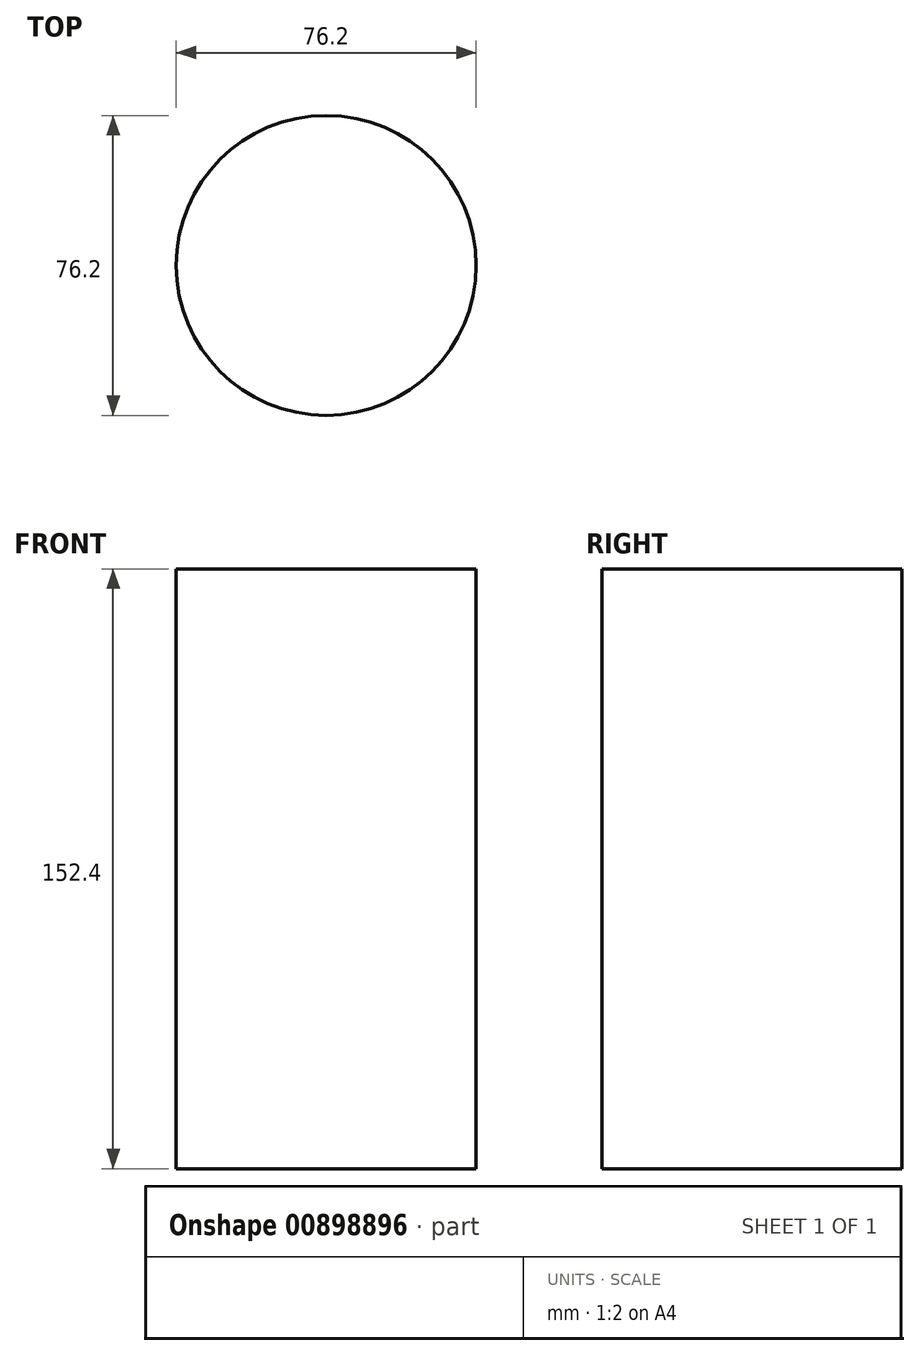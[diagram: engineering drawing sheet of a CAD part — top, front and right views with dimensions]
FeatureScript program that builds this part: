
annotation { "Feature Type Name" : "Feature", "Feature Type Description" : "" }
export const myFeature = defineFeature(function(context is Context, id is Id, definition is map)
    precondition{}
    {
        {
            var Q0;
            Q0=qCreatedBy(makeId("Top.planeOp"),FACE);
            var sketch = newSketch(context, id + "F0", { "sketchPlane" : qUnion([Q0])});
            skCircle(sketch, "E0", {"center": v(0, 0) * mm, "radius": 38.1 * mm});
            skSolve(sketch);
        }
        {
            var Q0;
            Q0 = qSketchRegion(id + "F0", true);
            extrude(context, id + "F1", {"entities" : qUnion([Q0]), "depth" : 152.4 * mm, "offsetDistance" : 25.4 * mm});
        }
    });
